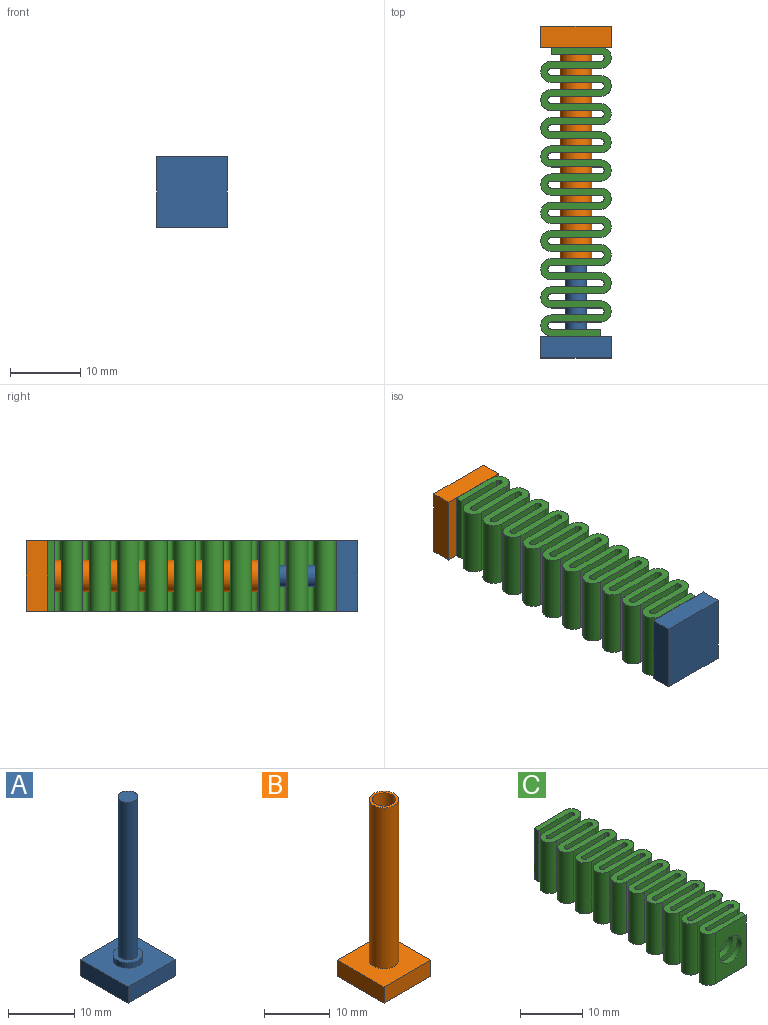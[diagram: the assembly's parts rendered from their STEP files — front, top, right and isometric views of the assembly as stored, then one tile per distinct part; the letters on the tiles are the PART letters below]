
ASSEMBLY  parts=3 mates=2
PART A: 10 faces, bbox 10x10x33 mm
  f0: cylinder r=1.5mm len=29mm, axis (0,0,-1), area 273.3mm2, adj f1,f3
  f1: plane 3x3mm, normal (0,0,1), area 7.1mm2, adj f0
  f2: cylinder r=2.25mm len=4.5mm, axis (0,0,-1), area 14.1mm2, adj f3,f9
  f3: plane 4.5x4.5mm, normal (0,0,1), area 8.8mm2, adj f0,f2
  f4: plane 10x3mm, normal (1,0,0), area 30mm2, adj f5,f7,f8,f9
  f5: plane 10x3mm, normal (0,1,0), area 30mm2, adj f4,f6,f8,f9
  f6: plane 10x3mm, normal (-1,0,0), area 30mm2, adj f5,f7,f8,f9
  f7: plane 10x3mm, normal (0,-1,0), area 30mm2, adj f4,f6,f8,f9
  f8: plane 10x10mm, normal (0,0,-1), area 100mm2, adj f4,f5,f6,f7
  f9: plane 10x10mm, normal (0,0,1), area 84.1mm2, adj f2,f4,f5,f6,f7
PART B: 10 faces, bbox 10x10x33 mm
  f0: cylinder r=1.75mm len=30mm, axis (0,0,-1), area 329.9mm2, adj f2,f9
  f1: cylinder r=2.25mm len=30mm, axis (0,0,-1), area 424.1mm2, adj f2,f3
  f2: plane 4.5x4.5mm, normal (0,0,1), area 6.3mm2, adj f0,f1
  f3: plane 10x10mm, normal (0,0,1), area 84.1mm2, adj f1,f5,f6,f7,f8
  f4: plane 10x10mm, normal (0,0,-1), area 100mm2, adj f5,f6,f7,f8
  f5: plane 10x3mm, normal (0,-1,0), area 30mm2, adj f3,f4,f6,f8
  f6: plane 10x3mm, normal (-1,0,0), area 30mm2, adj f3,f4,f5,f7
  f7: plane 10x3mm, normal (0,1,0), area 30mm2, adj f3,f4,f6,f8
  f8: plane 10x3mm, normal (1,0,0), area 30mm2, adj f3,f4,f5,f7
  f9: plane 3.5x3.5mm, normal (0,0,1), area 9.6mm2, adj f0
PART C: 107 faces, bbox 10x41x10 mm
  f0: plane 10x1mm, normal (1,0,0), area 10mm2, adj f1,f8,f9,f10
  f1: plane 10x7mm, normal (0,1,0), area 50.4mm2, adj f0,f2,f9,f10,f105
  f2: cylinder r=0.5mm len=10mm, axis (0,0,-1), area 15.7mm2, adj f1,f3,f9,f10
  f3: plane 10x7mm, normal (0,-1,0), area 50.4mm2, adj f2,f4,f9,f10,f106
  f4: cylinder r=1.5mm len=10mm, axis (0,0,-1), area 47.1mm2, adj f3,f9,f10,f11
  f5: cylinder r=0.5mm len=10mm, axis (0,0,-1), area 15.7mm2, adj f6,f9,f10,f18
  f6: plane 10x7mm, normal (0,1,0), area 50.4mm2, adj f5,f7,f9,f10,f106
  f7: cylinder r=1.5mm len=10mm, axis (0,0,-1), area 47.1mm2, adj f6,f8,f9,f10
  f8: plane 10x7mm, normal (0,-1,0), area 50.4mm2, adj f0,f7,f9,f10,f105
  f9: plane 41x10mm, normal (0,0,1), area 209.8mm2, adj f0,f1,f2,f3,f4,f5,f6,f7
  f10: plane 41x10mm, normal (0,0,-1), area 209.8mm2, adj f0,f1,f2,f3,f4,f5,f6,f7
  f11: plane 10x7mm, normal (0,1,0), area 50.4mm2, adj f4,f9,f10,f12,f103
  f12: cylinder r=0.5mm len=10mm, axis (0,0,-1), area 15.7mm2, adj f9,f10,f11,f13
  f13: plane 10x7mm, normal (0,-1,0), area 50.4mm2, adj f9,f10,f12,f14,f104
  f14: cylinder r=1.5mm len=10mm, axis (0,0,-1), area 47.1mm2, adj f9,f10,f13,f19
  f15: cylinder r=0.5mm len=10mm, axis (0,0,-1), area 15.7mm2, adj f9,f10,f16,f26
  f16: plane 10x7mm, normal (0,1,0), area 50.4mm2, adj f9,f10,f15,f17,f104
  f17: cylinder r=1.5mm len=10mm, axis (0,0,-1), area 47.1mm2, adj f9,f10,f16,f18
  f18: plane 10x7mm, normal (0,-1,0), area 50.4mm2, adj f5,f9,f10,f17,f103
  f19: plane 10x7mm, normal (0,1,0), area 50.4mm2, adj f9,f10,f14,f20,f101
  f20: cylinder r=0.5mm len=10mm, axis (0,0,-1), area 15.7mm2, adj f9,f10,f19,f21
  f21: plane 10x7mm, normal (0,-1,0), area 50.4mm2, adj f9,f10,f20,f22,f102
  f22: cylinder r=1.5mm len=10mm, axis (0,0,-1), area 47.1mm2, adj f9,f10,f21,f27
  f23: cylinder r=0.5mm len=10mm, axis (0,0,-1), area 15.7mm2, adj f9,f10,f24,f34
  f24: plane 10x7mm, normal (0,1,0), area 50.4mm2, adj f9,f10,f23,f25,f102
  f25: cylinder r=1.5mm len=10mm, axis (0,0,-1), area 47.1mm2, adj f9,f10,f24,f26
  f26: plane 10x7mm, normal (0,-1,0), area 50.4mm2, adj f9,f10,f15,f25,f101
  f27: plane 10x7mm, normal (0,1,0), area 50.4mm2, adj f9,f10,f22,f28,f99
  f28: cylinder r=0.5mm len=10mm, axis (0,0,-1), area 15.7mm2, adj f9,f10,f27,f29
  f29: plane 10x7mm, normal (0,-1,0), area 50.4mm2, adj f9,f10,f28,f30,f100
  f30: cylinder r=1.5mm len=10mm, axis (0,0,-1), area 47.1mm2, adj f9,f10,f29,f35
  f31: cylinder r=0.5mm len=10mm, axis (0,0,-1), area 15.7mm2, adj f9,f10,f32,f42
  f32: plane 10x7mm, normal (0,1,0), area 50.4mm2, adj f9,f10,f31,f33,f100
  f33: cylinder r=1.5mm len=10mm, axis (0,0,-1), area 47.1mm2, adj f9,f10,f32,f34
  f34: plane 10x7mm, normal (0,-1,0), area 50.4mm2, adj f9,f10,f23,f33,f99
  f35: plane 10x7mm, normal (0,1,0), area 50.4mm2, adj f9,f10,f30,f36,f97
  f36: cylinder r=0.5mm len=10mm, axis (0,0,-1), area 15.7mm2, adj f9,f10,f35,f37
  f37: plane 10x7mm, normal (0,-1,0), area 50.4mm2, adj f9,f10,f36,f38,f98
  f38: cylinder r=1.5mm len=10mm, axis (0,0,-1), area 47.1mm2, adj f9,f10,f37,f43
  f39: cylinder r=0.5mm len=10mm, axis (0,0,-1), area 15.7mm2, adj f9,f10,f40,f50
  f40: plane 10x7mm, normal (0,1,0), area 50.4mm2, adj f9,f10,f39,f41,f98
  f41: cylinder r=1.5mm len=10mm, axis (0,0,-1), area 47.1mm2, adj f9,f10,f40,f42
  f42: plane 10x7mm, normal (0,-1,0), area 50.4mm2, adj f9,f10,f31,f41,f97
  f43: plane 10x7mm, normal (0,1,0), area 50.4mm2, adj f9,f10,f38,f44,f95
  f44: cylinder r=0.5mm len=10mm, axis (0,0,-1), area 15.7mm2, adj f9,f10,f43,f45
  f45: plane 10x7mm, normal (0,-1,0), area 50.4mm2, adj f9,f10,f44,f46,f96
  f46: cylinder r=1.5mm len=10mm, axis (0,0,-1), area 47.1mm2, adj f9,f10,f45,f51
  f47: cylinder r=0.5mm len=10mm, axis (0,0,-1), area 15.7mm2, adj f9,f10,f48,f58
  f48: plane 10x7mm, normal (0,1,0), area 50.4mm2, adj f9,f10,f47,f49,f96
  f49: cylinder r=1.5mm len=10mm, axis (0,0,-1), area 47.1mm2, adj f9,f10,f48,f50
  f50: plane 10x7mm, normal (0,-1,0), area 50.4mm2, adj f9,f10,f39,f49,f95
  f51: plane 10x7mm, normal (0,1,0), area 50.4mm2, adj f9,f10,f46,f52,f93
  f52: cylinder r=0.5mm len=10mm, axis (0,0,-1), area 15.7mm2, adj f9,f10,f51,f53
  f53: plane 10x7mm, normal (0,-1,0), area 50.4mm2, adj f9,f10,f52,f54,f94
  f54: cylinder r=1.5mm len=10mm, axis (0,0,-1), area 47.1mm2, adj f9,f10,f53,f59
  f55: cylinder r=0.5mm len=10mm, axis (0,0,-1), area 15.7mm2, adj f9,f10,f56,f66
  f56: plane 10x7mm, normal (0,1,0), area 50.4mm2, adj f9,f10,f55,f57,f94
  f57: cylinder r=1.5mm len=10mm, axis (0,0,-1), area 47.1mm2, adj f9,f10,f56,f58
  f58: plane 10x7mm, normal (0,-1,0), area 50.4mm2, adj f9,f10,f47,f57,f93
  f59: plane 10x7mm, normal (0,1,0), area 50.4mm2, adj f9,f10,f54,f60,f91
  f60: cylinder r=0.5mm len=10mm, axis (0,0,-1), area 15.7mm2, adj f9,f10,f59,f61
  f61: plane 10x7mm, normal (0,-1,0), area 50.4mm2, adj f9,f10,f60,f62,f92
  f62: cylinder r=1.5mm len=10mm, axis (0,0,-1), area 47.1mm2, adj f9,f10,f61,f67
  f63: cylinder r=0.5mm len=10mm, axis (0,0,-1), area 15.7mm2, adj f9,f10,f64,f74
  f64: plane 10x7mm, normal (0,1,0), area 50.4mm2, adj f9,f10,f63,f65,f92
  f65: cylinder r=1.5mm len=10mm, axis (0,0,-1), area 47.1mm2, adj f9,f10,f64,f66
  f66: plane 10x7mm, normal (0,-1,0), area 50.4mm2, adj f9,f10,f55,f65,f91
  f67: plane 10x7mm, normal (0,1,0), area 50.4mm2, adj f9,f10,f62,f68,f89
  f68: cylinder r=0.5mm len=10mm, axis (0,0,-1), area 15.7mm2, adj f9,f10,f67,f69
  f69: plane 10x7mm, normal (0,-1,0), area 50.4mm2, adj f9,f10,f68,f70,f90
  f70: cylinder r=1.5mm len=10mm, axis (0,0,-1), area 47.1mm2, adj f9,f10,f69,f75
  f71: cylinder r=0.5mm len=10mm, axis (0,0,-1), area 15.7mm2, adj f9,f10,f72,f82
  f72: plane 10x7mm, normal (0,1,0), area 50.4mm2, adj f9,f10,f71,f73,f90
  f73: cylinder r=1.5mm len=10mm, axis (0,0,-1), area 47.1mm2, adj f9,f10,f72,f74
  f74: plane 10x7mm, normal (0,-1,0), area 50.4mm2, adj f9,f10,f63,f73,f89
  f75: plane 10x7mm, normal (0,1,0), area 50.4mm2, adj f9,f10,f70,f76,f87
  f76: cylinder r=0.5mm len=10mm, axis (0,0,-1), area 15.7mm2, adj f9,f10,f75,f77
  f77: plane 10x7mm, normal (0,-1,0), area 50.4mm2, adj f9,f10,f76,f78,f88
  f78: cylinder r=1.5mm len=10mm, axis (0,0,-1), area 47.1mm2, adj f9,f10,f77,f85
  f79: cylinder r=0.5mm len=10mm, axis (0,0,-1), area 15.7mm2, adj f9,f10,f80,f84
  f80: plane 10x7mm, normal (0,1,0), area 50.4mm2, adj f9,f10,f79,f81,f88
  f81: cylinder r=1.5mm len=10mm, axis (0,0,-1), area 47.1mm2, adj f9,f10,f80,f82
  f82: plane 10x7mm, normal (0,-1,0), area 50.4mm2, adj f9,f10,f71,f81,f87
  f83: plane 10x1mm, normal (-1,0,0), area 10mm2, adj f9,f10,f84,f85
  f84: plane 10x7mm, normal (0,-1,0), area 50.4mm2, adj f9,f10,f79,f83,f86
  f85: plane 10x7mm, normal (0,1,0), area 50.4mm2, adj f9,f10,f78,f83,f86
  f86: cylinder r=2.5mm len=5mm, axis (0,-1,0), area 15.7mm2, adj f84,f85
  f87: cylinder r=2.5mm len=5mm, axis (0,-1,0), area 15.7mm2, adj f75,f82
  f88: cylinder r=2.5mm len=5mm, axis (0,-1,0), area 15.7mm2, adj f77,f80
  f89: cylinder r=2.5mm len=5mm, axis (0,-1,0), area 15.7mm2, adj f67,f74
  f90: cylinder r=2.5mm len=5mm, axis (0,-1,0), area 15.7mm2, adj f69,f72
  f91: cylinder r=2.5mm len=5mm, axis (0,-1,0), area 15.7mm2, adj f59,f66
  f92: cylinder r=2.5mm len=5mm, axis (0,-1,0), area 15.7mm2, adj f61,f64
  f93: cylinder r=2.5mm len=5mm, axis (0,-1,0), area 15.7mm2, adj f51,f58
  f94: cylinder r=2.5mm len=5mm, axis (0,-1,0), area 15.7mm2, adj f53,f56
  f95: cylinder r=2.5mm len=5mm, axis (0,-1,0), area 15.7mm2, adj f43,f50
  f96: cylinder r=2.5mm len=5mm, axis (0,-1,0), area 15.7mm2, adj f45,f48
  f97: cylinder r=2.5mm len=5mm, axis (0,-1,0), area 15.7mm2, adj f35,f42
  f98: cylinder r=2.5mm len=5mm, axis (0,-1,0), area 15.7mm2, adj f37,f40
  f99: cylinder r=2.5mm len=5mm, axis (0,-1,0), area 15.7mm2, adj f27,f34
  f100: cylinder r=2.5mm len=5mm, axis (0,-1,0), area 15.7mm2, adj f29,f32
  f101: cylinder r=2.5mm len=5mm, axis (0,-1,0), area 15.7mm2, adj f19,f26
  f102: cylinder r=2.5mm len=5mm, axis (0,-1,0), area 15.7mm2, adj f21,f24
  f103: cylinder r=2.5mm len=5mm, axis (0,-1,0), area 15.7mm2, adj f11,f18
  f104: cylinder r=2.5mm len=5mm, axis (0,-1,0), area 15.7mm2, adj f13,f16
  f105: cylinder r=2.5mm len=5mm, axis (0,-1,0), area 15.7mm2, adj f1,f8
  f106: cylinder r=2.5mm len=5mm, axis (0,-1,0), area 15.7mm2, adj f3,f6
PLACE A rot(axis=(-1,0,0),90deg) t=(0,-44.09,0)mm
PLACE B rot(axis=(0,-0.71,0.71),180deg) t=(0,-3,0)mm
PLACE C t=(0,-44,-5)mm
MATE fastened C.f86 <-> B.f1  axis (0,1,0) through (0,-3,0)mm
MATE slider A.f0 <-> B.f0  axis (0,1,0) through (0,-14.09,0)mm
